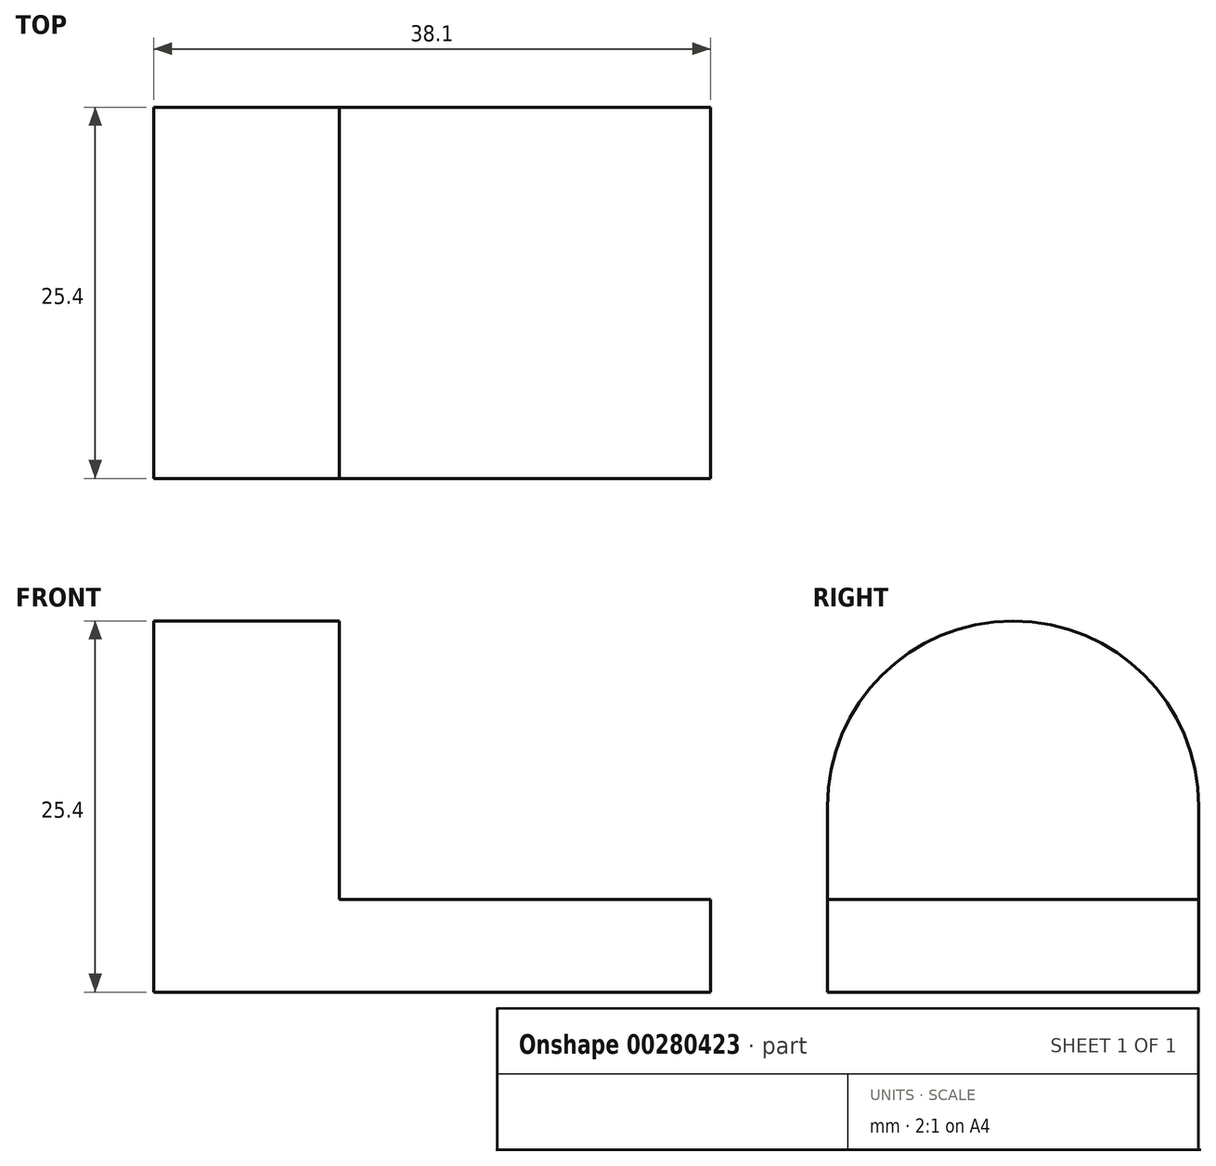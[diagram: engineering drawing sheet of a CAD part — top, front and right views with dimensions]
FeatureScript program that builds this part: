
annotation { "Feature Type Name" : "Feature", "Feature Type Description" : "" }
export const myFeature = defineFeature(function(context is Context, id is Id, definition is map)
    precondition{}
    {
        {
            var Q0;
            Q0=qCreatedBy(makeId("Front.planeOp"),FACE);
            var sketch = newSketch(context, id + "F0", { "sketchPlane" : qUnion([Q0])});
            skLineSegment(sketch, "E0", {"start": v(0, 0) * mm, "end": v(38.1, 0) * mm});
            skLineSegment(sketch, "E1", {"start": v(38.1, 0) * mm, "end": v(38.1, 6.35) * mm});
            skLineSegment(sketch, "E2", {"start": v(38.1, 6.35) * mm, "end": v(12.7, 6.35) * mm});
            skLineSegment(sketch, "E3", {"start": v(12.7, 6.35) * mm, "end": v(12.7, 25.4) * mm});
            skLineSegment(sketch, "E4", {"start": v(12.7, 25.4) * mm, "end": v(0, 25.4) * mm});
            skLineSegment(sketch, "E5", {"start": v(0, 25.4) * mm, "end": v(0, 0) * mm});
            skSolve(sketch);
        }
        {
            var Q0;
            Q0 = qSketchRegion(id + "F0", true);
            extrude(context, id + "F1", {"entities" : qUnion([Q0]), "depth" : 25.4 * mm, "symmetric" : true});
        }
        {
            var Q0;
            Q0=makeQuery(id+"F1.opExtrude","CAP_EDGE",EDGE,{"disambiguationData":[OSD([sQuery(id+"F0.wireOp",EDGE,"E4")])],"isStart":false});
            fillet(context, id + "F2", {"entities" : qUnion([Q0]), "radius" : 12.7 * mm, "tangentPropagation" : true, "allowEdgeOverflow" : false});
        }
        {
            var Q0;
            Q0=makeQuery(id+"F1.opExtrude","CAP_EDGE",EDGE,{"disambiguationData":[OSD([sQuery(id+"F0.wireOp",EDGE,"E4")])],"isStart":true});
            fillet(context, id + "F3", {"entities" : qUnion([Q0]), "radius" : 12.7 * mm, "tangentPropagation" : true, "allowEdgeOverflow" : false});
        }
    });
